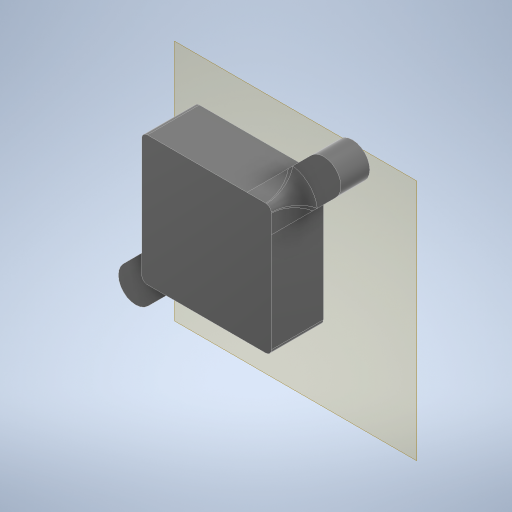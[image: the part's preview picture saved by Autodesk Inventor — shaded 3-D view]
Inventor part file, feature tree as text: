
AUTODESK INVENTOR PART (.ipt)
format: ipt  version: 2023 (Build 270158000, 158)  size: 356,352 bytes
history: native  units: in
note: dims shown in document units (in); Inventor stores cm internally (conversion verified against a paired STEP export)
features: reference x10, extrude x2, sketch x2, other x2, plane x1, fillet x1
ambient origin geometry x8: Origin, YZ Plane, XZ Plane, XY Plane, X Axis, Y Axis, Z Axis, Center Point
bodies: Solid1 (feature_tree), Body_Normal_2 (feature_tree)
feature tree (18):
  plane  "Work Plane1"
  extrude  "Extrusion1"  Depth=0.4724in
  extrude  "Extrusion2"  Depth=0.315in
  fillet  "Fillet1"  Radius=0.0787in
  sketch  "Sketch1"  dims[d0=0.4724in d1=0.4724in]
  reference  "Reference1"
  reference  "Reference2"
  reference  "Reference3"
  reference  "Reference4"
  reference  "Reference5"
  reference  "Reference6"
  reference  "Reference7"
  reference  "Reference8"
  reference  "Reference9"
  reference  "Reference10"
  sketch  "Sketch2"  dims[d2=1.7717in d3=1.7717in d4=0.0787in d5=0.7087in d6=0.0in d7=1.5748in d9=360.0deg d11=0.315in d12=0.0in d13=0.315in]
  other  "<userpath>\Downloads\frame\parts\Reader\RF622A.iam"
  other  "RF622A.iam"
